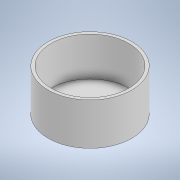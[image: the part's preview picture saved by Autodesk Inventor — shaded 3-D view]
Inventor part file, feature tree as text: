
AUTODESK INVENTOR PART (.ipt)
format: ipt  version: 2022 (Build 260153000, 153)  size: 104,448 bytes
history: native  units: mm
features: extrude x2, sketch x2, projected_geometry x1
ambient origin geometry x8: Origin, YZ Plane, XZ Plane, XY Plane, X Axis, Y Axis, Z Axis, Center Point
bodies: Solid1 (feature_tree)
feature tree (5):
  extrude  "Extrusion1"  Depth=1.0mm TaperAngle=0.0deg
  extrude  "Extrusion2"  Depth=13.0mm TaperAngle=0.0deg
  sketch  "Sketch1"  dims[d0=28.0mm d1=1.0mm d2=0.0mm]
  sketch  "Sketch2"  dims[d3=1.0mm d4=13.0mm d5=0.0mm]
  projected_geometry  "Projected Loop1"
